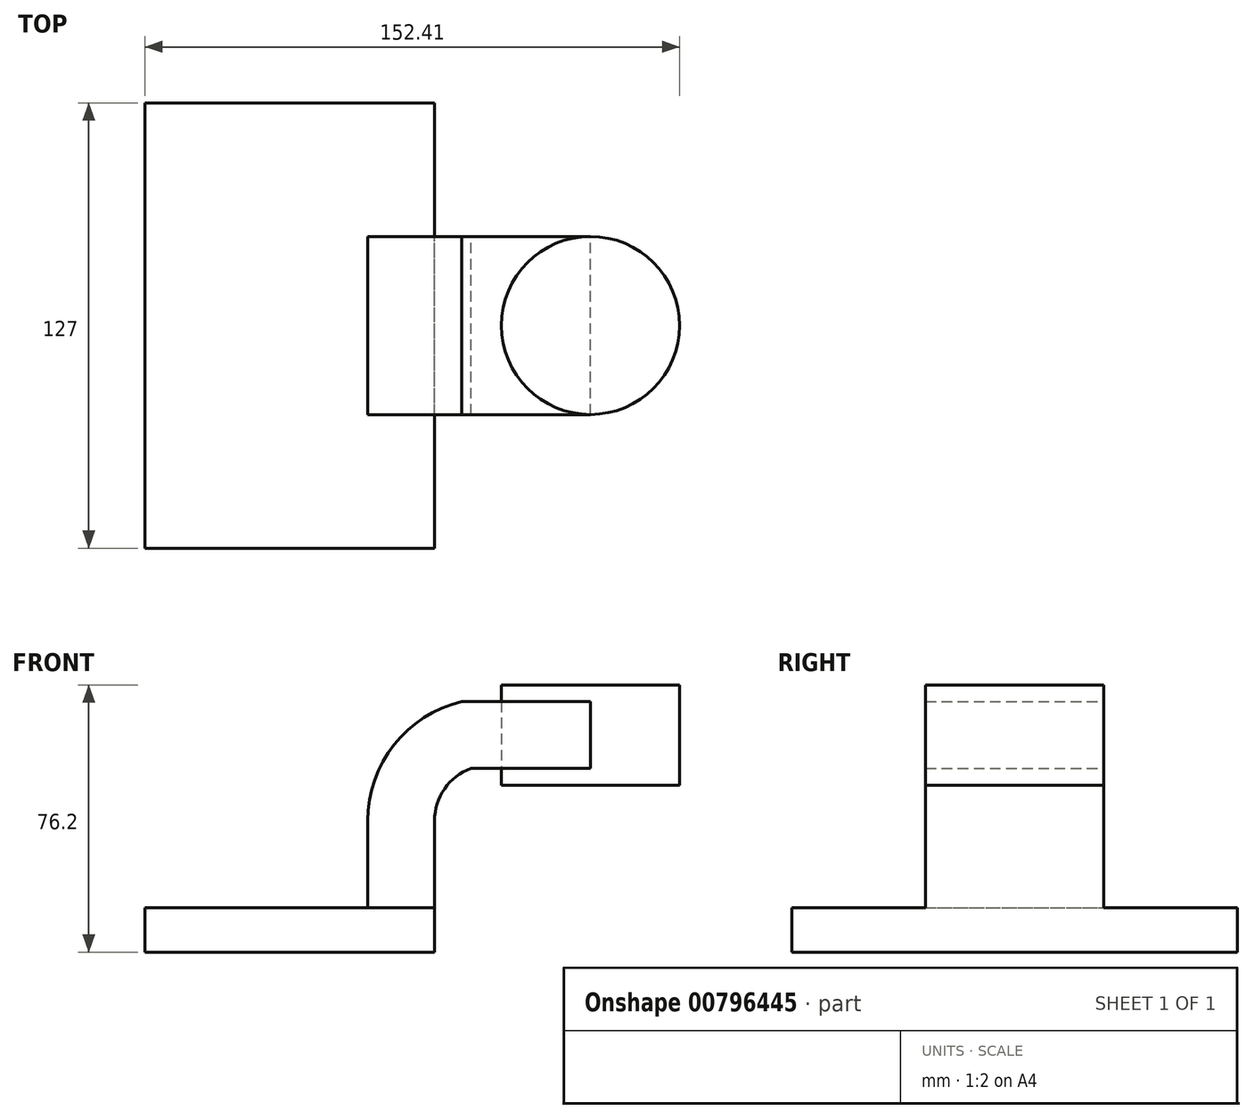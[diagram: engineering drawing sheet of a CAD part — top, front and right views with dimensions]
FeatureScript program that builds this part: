
annotation { "Feature Type Name" : "Feature", "Feature Type Description" : "" }
export const myFeature = defineFeature(function(context is Context, id is Id, definition is map)
    precondition{}
    {
        {
            var Q0;
            Q0=qCreatedBy(makeId("Front.planeOp"),FACE);
            var sketch = newSketch(context, id + "F0", { "sketchPlane" : qUnion([Q0])});
            skLineSegment(sketch, "E0.bottom", {"start": v(41.27, 6.35) * mm, "end": v(-41.28, 6.35) * mm});
            skLineSegment(sketch, "E0.top", {"start": v(41.28, -6.35) * mm, "end": v(-41.27, -6.35) * mm});
            skLineSegment(sketch, "E0.left", {"start": v(41.28, 6.35) * mm, "end": v(41.28, -6.35) * mm});
            skLineSegment(sketch, "E0.right", {"start": v(-41.28, 6.35) * mm, "end": v(-41.27, -6.35) * mm});
            skPoint(sketch, "E0.middle", {"position": v(0, 0) * mm});
            skPoint(sketch, "E1.middle", {"position": v(100.74, 46.05) * mm});
            skLineSegment(sketch, "E2.bottom", {"start": v(60.33, 41.28) * mm, "end": v(111.12, 41.28) * mm});
            skLineSegment(sketch, "E2.top", {"start": v(60.33, 69.85) * mm, "end": v(111.12, 69.85) * mm});
            skLineSegment(sketch, "E2.left", {"start": v(60.33, 41.28) * mm, "end": v(60.33, 69.85) * mm});
            skLineSegment(sketch, "E2.right", {"start": v(111.13, 41.28) * mm, "end": v(111.13, 69.85) * mm});
            skPoint(sketch, "E2.middle", {"position": v(85.73, 55.56) * mm});
            skPoint(sketch, "E3.endSnap0", {"position": v(85.73, 41.28) * mm});
            skLineSegment(sketch, "E4", {"start": v(41.27, 6.35) * mm, "end": v(41.27, 31.15) * mm});
            skArc(sketch, "E5", {"start": v(41.28, 31.15) * mm, "mid": v(44.13, 40.23) * mm, "end": v(51.68, 46.05) * mm});
            skLineSegment(sketch, "E6", {"start": v(51.68, 46.05) * mm, "end": v(85.72, 46.05) * mm});
            skLineSegment(sketch, "E7.0", {"start": v(48.96, 65.1) * mm, "end": v(85.72, 65.1) * mm});
            skArc(sketch, "E7.1", {"start": v(22.23, 31.15) * mm, "mid": v(29.71, 52.76) * mm, "end": v(48.96, 65.1) * mm});
            skLineSegment(sketch, "E7.2", {"start": v(22.23, 6.35) * mm, "end": v(22.23, 31.15) * mm});
            skLineSegment(sketch, "E8", {"start": v(85.73, 41.28) * mm, "end": v(85.73, 69.85) * mm});
            skFitSpline(sketch, "E9", {"points": [v(-41.28, 6.35) * mm, v(48.96, 65.1) * mm], "startDerivative": vector(-1.39, 133.08) * mm, "endDerivative": vector(132.88, -0.6) * mm});
            skSolve(sketch);
        }
        {
            var Q0;
            Q0=makeQuery(id+"F0.imprint","IMPRINT",FACE,{"disambiguationData":[TD([[makeQuery(id+"F0.imprint","IMPRINT",EDGE,{"derivedFrom":sQuery(id+"F0.wireOp",EDGE,"E0.top")}),-1.0]])]});
            extrude(context, id + "F1", {"entities" : qUnion([Q0]), "endBound" : BoundingType.SYMMETRIC, "depth" : 127 * mm, "offsetDistance" : 25.4 * mm});
        }
        {
            var Q0;
            {var subQ1=sQuery(id+"F0.wireOp",EDGE,"E4");Q0=makeQuery(id+"F0.imprint","IMPRINT",FACE,{"disambiguationData":[TD([[makeQuery(id+"F0.imprint","IMPRINT",EDGE,{"derivedFrom":subQ1}),1.0]])]});}
            var Q1;
            {var subQ0=sQuery(id+"F0.wireOp",EDGE,"E6");var subQ1=sQuery(id+"F0.wireOp",EDGE,"E2.left");var subQ2=makeQuery(id+"F0.imprint","INTERSECT",VERTEX,{"derivedFrom":[subQ1,subQ0]});Q1=makeQuery(id+"F0.imprint","IMPRINT",FACE,{"disambiguationData":[TD([[makeQuery(id+"F0.imprint","IMPRINT",EDGE,{"disambiguationData":[TD([[subQ2,-1.0]])],"derivedFrom":subQ1}),-1.0]])]});}
            extrude(context, id + "F2", {"entities" : qUnion([Q0, Q1]), "operationType" : NewBodyOperationType.ADD, "endBound" : BoundingType.SYMMETRIC, "depth" : 50.8 * mm, "offsetDistance" : 25.4 * mm});
        }
        {
            var Q0;
            Q0=makeQuery(id+"F0.imprint","IMPRINT",FACE,{"disambiguationData":[TD([[makeQuery(id+"F0.imprint","IMPRINT",EDGE,{"derivedFrom":sQuery(id+"F0.wireOp",EDGE,"E7.1")}),1.0]])]});
            extrude(context, id + "F3", {"entities" : qUnion([Q0]), "operationType" : NewBodyOperationType.ADD, "endBound" : BoundingType.SYMMETRIC, "depth" : 15.88 * mm, "offsetDistance" : 25.4 * mm});
        }
        {
            var Q0;
            {var subQ0=sQuery(id+"F0.wireOp",EDGE,"E2.right");Q0=makeQuery(id+"F0.imprint","IMPRINT",FACE,{"disambiguationData":[TD([[makeQuery(id+"F0.imprint","IMPRINT",EDGE,{"derivedFrom":subQ0}),1.0]])]});}
            var Q1;
            Q1=sQuery(id+"F0.wireOp",EDGE,"E8");
            revolve(context, id + "F4", {"surfaceOperationType" : NewSurfaceOperationType.NEW, "entities" : qUnion([Q0]), "axis" : qUnion([Q1]), "revolveType" : RevolveType.FULL});
        }
    });
